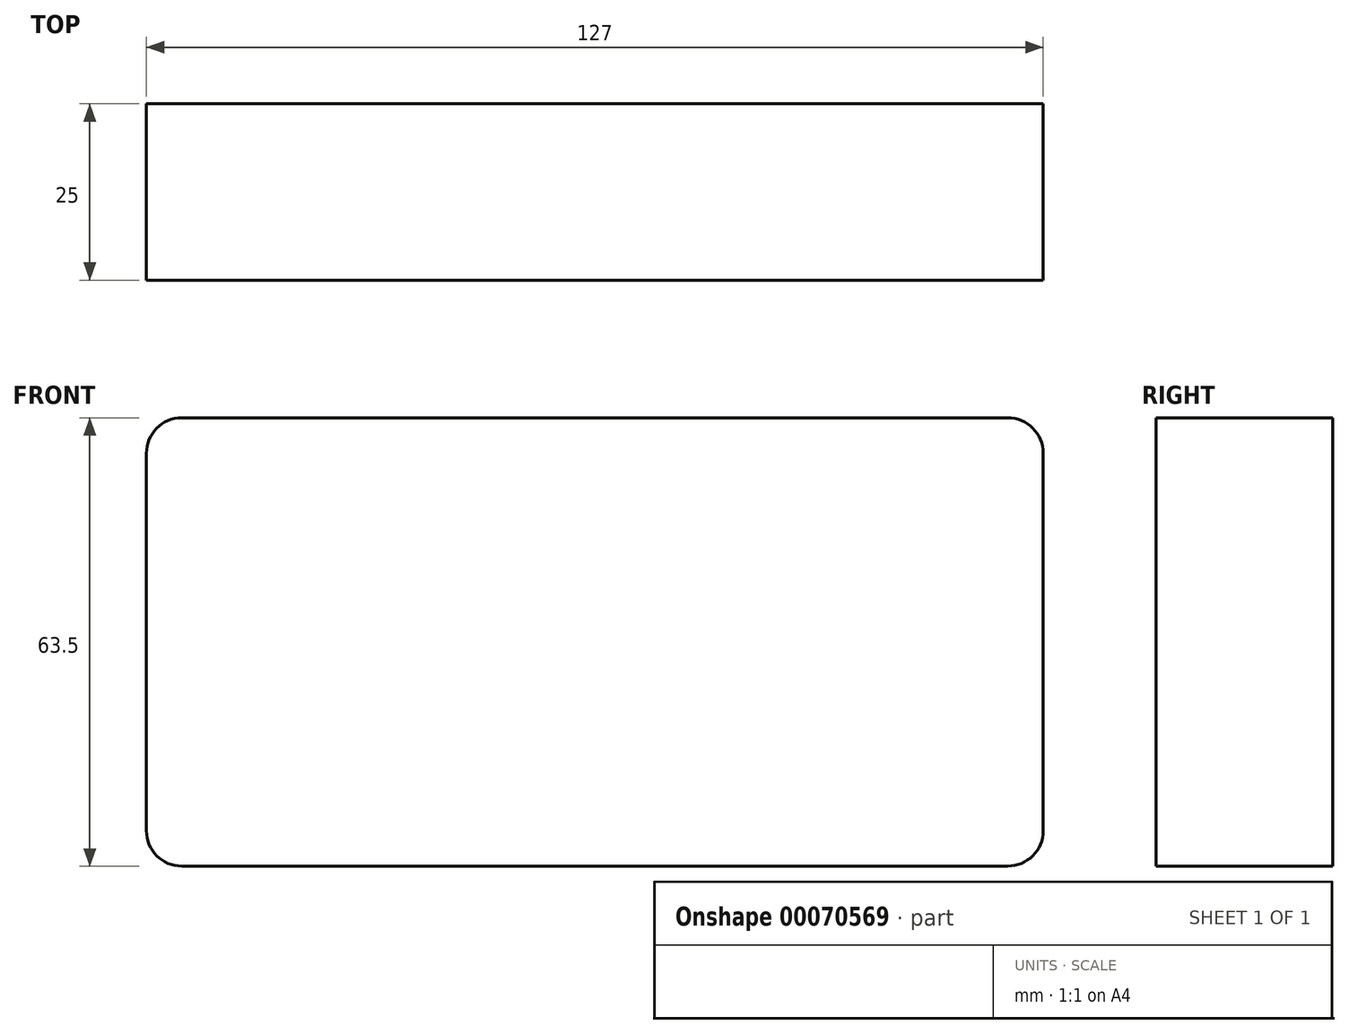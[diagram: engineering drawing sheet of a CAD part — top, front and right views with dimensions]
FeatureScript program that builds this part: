
annotation { "Feature Type Name" : "Feature", "Feature Type Description" : "" }
export const myFeature = defineFeature(function(context is Context, id is Id, definition is map)
    precondition{}
    {
        {
            var Q0;
            Q0=qCreatedBy(makeId("Front.planeOp"),FACE);
            var sketch = newSketch(context, id + "F0", { "sketchPlane" : qUnion([Q0])});
            skLineSegment(sketch, "E0.bottom", {"start": v(0, 0) * mm, "end": v(127, 0) * mm});
            skLineSegment(sketch, "E0.top", {"start": v(0, 63.5) * mm, "end": v(127, 63.5) * mm});
            skLineSegment(sketch, "E0.left", {"start": v(0, 0) * mm, "end": v(0, 63.5) * mm});
            skLineSegment(sketch, "E0.right", {"start": v(127, 0) * mm, "end": v(127, 63.5) * mm});
            skSolve(sketch);
        }
        {
            var Q0;
            Q0 = qSketchRegion(id + "F0", true);
            extrude(context, id + "F1", {"entities" : qUnion([Q0]), "depth" : 25 * mm});
        }
        {
            var Q0;
            Q0=makeQuery(id+"F1.opExtrude","SWEPT_EDGE",EDGE,{"disambiguationData":[OSD([sQuery(id+"F0.wireOp",EDGE,"E0.top"),sQuery(id+"F0.wireOp",EDGE,"E0.left")])]});
            var Q1;
            Q1=makeQuery(id+"F1.opExtrude","SWEPT_EDGE",EDGE,{"disambiguationData":[OSD([sQuery(id+"F0.wireOp",EDGE,"E0.top"),sQuery(id+"F0.wireOp",EDGE,"E0.right")])]});
            var Q2;
            Q2=makeQuery(id+"F1.opExtrude","SWEPT_EDGE",EDGE,{"disambiguationData":[OSD([sQuery(id+"F0.wireOp",EDGE,"E0.bottom"),sQuery(id+"F0.wireOp",EDGE,"E0.left")])]});
            var Q3;
            Q3=makeQuery(id+"F1.opExtrude","SWEPT_EDGE",EDGE,{"disambiguationData":[OSD([sQuery(id+"F0.wireOp",EDGE,"E0.bottom"),sQuery(id+"F0.wireOp",EDGE,"E0.right")])]});
            fillet(context, id + "F2", {"entities" : qUnion([Q0, Q1, Q2, Q3]), "radius" : 5 * mm, "tangentPropagation" : true, "allowEdgeOverflow" : false});
        }
    });
